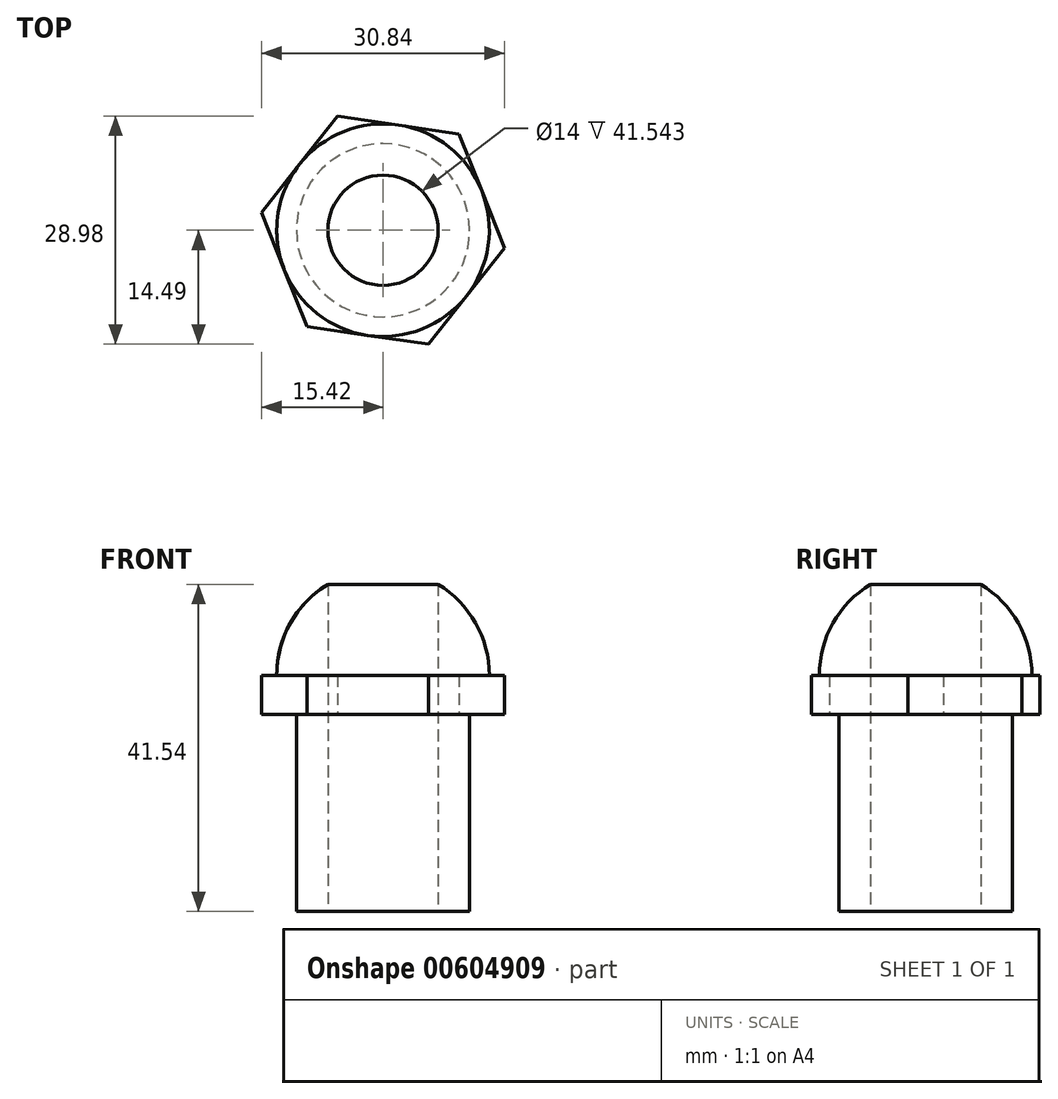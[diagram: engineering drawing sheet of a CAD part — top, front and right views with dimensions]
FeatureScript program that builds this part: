
annotation { "Feature Type Name" : "Feature", "Feature Type Description" : "" }
export const myFeature = defineFeature(function(context is Context, id is Id, definition is map)
    precondition{}
    {
        {
            var Q0;
            Q0=qCreatedBy(makeId("Top.planeOp"),FACE);
            var sketch = newSketch(context, id + "F0", { "sketchPlane" : qUnion([Q0])});
            skCircle(sketch, "E0", {"center": v(0, 0) * mm, "radius": 11 * mm});
            skSolve(sketch);
        }
        {
            var Q0;
            Q0 = qSketchRegion(id + "F0", true);
            extrude(context, id + "F1", {"entities" : qUnion([Q0]), "depth" : 25 * mm, "offsetDistance" : 25 * mm});
        }
        {
            var Q0;
            Q0=makeQuery(id+"F1.opExtrude","CAP_FACE",FACE,{"disambiguationData":[OSD([sQuery(id+"F0.wireOp",EDGE,"E0")])],"isStart":false});
            var sketch = newSketch(context, id + "F2", { "sketchPlane" : qUnion([Q0])});
            skCircle(sketch, "E1.cCircle", {"center": v(0, 0) * mm, "radius": 13.5 * mm, "construction": true});
            skLineSegment(sketch, "E1.0", {"start": v(9.67, 12.23) * mm, "end": v(15.42, -2.26) * mm});
            skLineSegment(sketch, "E1.1", {"start": v(15.42, -2.26) * mm, "end": v(5.75, -14.49) * mm});
            skLineSegment(sketch, "E1.2", {"start": v(5.75, -14.49) * mm, "end": v(-9.67, -12.23) * mm});
            skLineSegment(sketch, "E1.3", {"start": v(-9.67, -12.23) * mm, "end": v(-15.42, 2.26) * mm});
            skLineSegment(sketch, "E1.4", {"start": v(-15.42, 2.26) * mm, "end": v(-5.75, 14.49) * mm});
            skLineSegment(sketch, "E1.5", {"start": v(-5.75, 14.49) * mm, "end": v(9.67, 12.23) * mm});
            skPoint(sketch, "E1.0.midPoint", {"position": v(12.55, 4.98) * mm});
            skSolve(sketch);
        }
        {
            var Q0;
            Q0 = qSketchRegion(id + "F2", true);
            extrude(context, id + "F3", {"entities" : qUnion([Q0]), "operationType" : NewBodyOperationType.ADD, "depth" : 5 * mm, "offsetDistance" : 25 * mm});
        }
        {
            var Q0;
            Q0=qCreatedBy(makeId("Front.planeOp"),FACE);
            var sketch = newSketch(context, id + "F4", { "sketchPlane" : qUnion([Q0])});
            skLineSegment(sketch, "E2", {"start": v(0, 30) * mm, "end": v(0, 43.5) * mm, "construction": true});
            skArc(sketch, "E3", {"start": v(-13.5, 30) * mm, "mid": v(-9.55, 39.55) * mm, "end": v(0, 43.5) * mm});
            skLineSegment(sketch, "E4", {"start": v(0, 43.5) * mm, "end": v(0, 30) * mm});
            skLineSegment(sketch, "E5", {"start": v(0, 30) * mm, "end": v(-13.5, 30) * mm});
            skLineSegment(sketch, "E6", {"start": v(0, 0) * mm, "end": v(0, 54) * mm, "construction": true});
            skSolve(sketch);
        }
        {
            var Q0;
            Q0 = qSketchRegion(id + "F4", true);
            var Q1;
            Q1=sQuery(id+"F4.wireOp",EDGE,"E6");
            revolve(context, id + "F5", {"operationType" : NewBodyOperationType.ADD, "entities" : qUnion([Q0]), "axis" : qUnion([Q1]), "revolveType" : RevolveType.FULL});
        }
        {
            var Q0;
            Q0=makeQuery(id+"F1.opExtrude","CAP_FACE",FACE,{"disambiguationData":[OSD([sQuery(id+"F0.wireOp",EDGE,"E0")])],"isStart":true});
            var sketch = newSketch(context, id + "F6", { "sketchPlane" : qUnion([Q0])});
            skCircle(sketch, "E7", {"center": v(0, 0) * mm, "radius": 7 * mm});
            skSolve(sketch);
        }
        {
            var Q0;
            Q0 = qSketchRegion(id + "F6", true);
            extrude(context, id + "F7", {"entities" : qUnion([Q0]), "operationType" : NewBodyOperationType.REMOVE, "endBound" : BoundingType.THROUGH_ALL, "oppositeDirection" : true, "depth" : 25 * mm, "offsetDistance" : 25 * mm});
        }
    });
